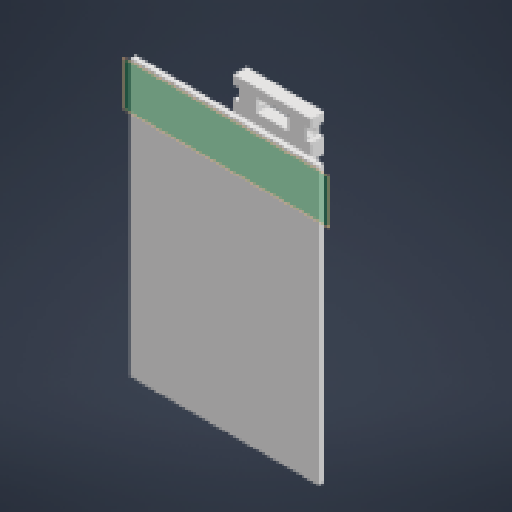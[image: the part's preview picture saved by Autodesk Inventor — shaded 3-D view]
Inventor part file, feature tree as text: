
AUTODESK INVENTOR PART (.ipt)
format: ipt  version: 2024 (Build 280153000, 153)  size: 163,328 bytes
history: native  units: in
note: dims shown in document units (in); Inventor stores cm internally (conversion verified against a paired STEP export)
features: reference x7, other x5, sketch x4, extrude x4, fillet x1, plane x1
ambient origin geometry x8: Origin, YZ Plane, XZ Plane, XY Plane, X Axis, Y Axis, Z Axis, Center Point
bodies: Solid1 (feature_tree)
feature tree (22):
  sketch  "Sketch1"  dims[d0=0.0157in d1=0.4646in]
  other  "Work Point1"
  extrude  "Extrusion1"  Depth=0.4646in
  extrude  "Extrusion2"  Depth=1.0in TaperAngle=0.0deg
  extrude  "Extrusion3"  Depth=0.1378in TaperAngle=0.0deg
  extrude  "Extrusion4"  Depth=0.1378in TaperAngle=0.0deg
  fillet  "Fillet1"  Radius=0.0394in
  plane  "Work Plane1"
  reference  "Reference1"
  reference  "Reference2"
  reference  "Reference3"
  reference  "Reference4"
  reference  "Reference5"
  reference  "Reference6"
  sketch  "Sketch2"  dims[d2=1.0in d3=0.0in d4=1.0in d5=0.0in]
  reference  "Reference7"
  sketch  "Sketch3"  dims[d6=0.2598in d7=0.1378in d8=0.0in]
  sketch  "Sketch4"  dims[d9=0.2598in d10=0.1378in d11=0.0in d12=0.0394in]
  other  "<userpath>\Desktop\SeniorDesign\Head_V3\Head_V3_Assembly.iam"
  other  "Head_V3_Assembly.iam"
  other  "Emeet_Camera:1"
  other  "Assembly1"
